# Revit family: Sanitary_Other_Encon-Safety_Wall-Mount-Eyewash-SS-Bowl
name_source: partatom
category: Plumbing Fixtures
units: mm (PartAtom-declared; Revit-internal decimal feet)

## family parameters
Cut with Voids When Loaded = No
Host = Face
OmniClass Number = 23.45.05.14.24
OmniClass Title = Eye Wash Fountains
Part Type = Normal
Room Calculation Point = No
Round Connector Dimension = Use Diameter
Shared = No

## types (1)
- 01045001
    Assembly Code = D2010600
    Bowl Material = Encon Safety Products - Metal - Stainless Steel
    CWFU = 0
    Default Elevation = 48"
    Description = Wall mount eyewash SS bowl, 2.4 gpm Acetal eyewash
    Drain Type = FNPT
    Edition number = 1
    Flow = 3 GPM
    Fluid out Diameter = 1 1/2"
    Heads Material = Encon Safety Products - Plastic - Acetal - Yellow
    Height = 8"
    Keynote = 15410
    Manufacturer = Encon Safety Products
    Model = 01045001
    Pedestal Material = Encon Safety Products - Metal - Stainless Steel
    Piping Material = Encon Safety Products - Metal - Stainless Steel
    Product Guid = 68e39ca3-a789-45c7-8317-a775f6945996
    Product data url = https://www.bimobject.com
    Supply Diameter = 1/2"
    URL = https://enconsafety.com
    Width = 16"

## geometry (parser evidence)
native form markers: Sweep x2
no freeform markers — native parametric forms only
